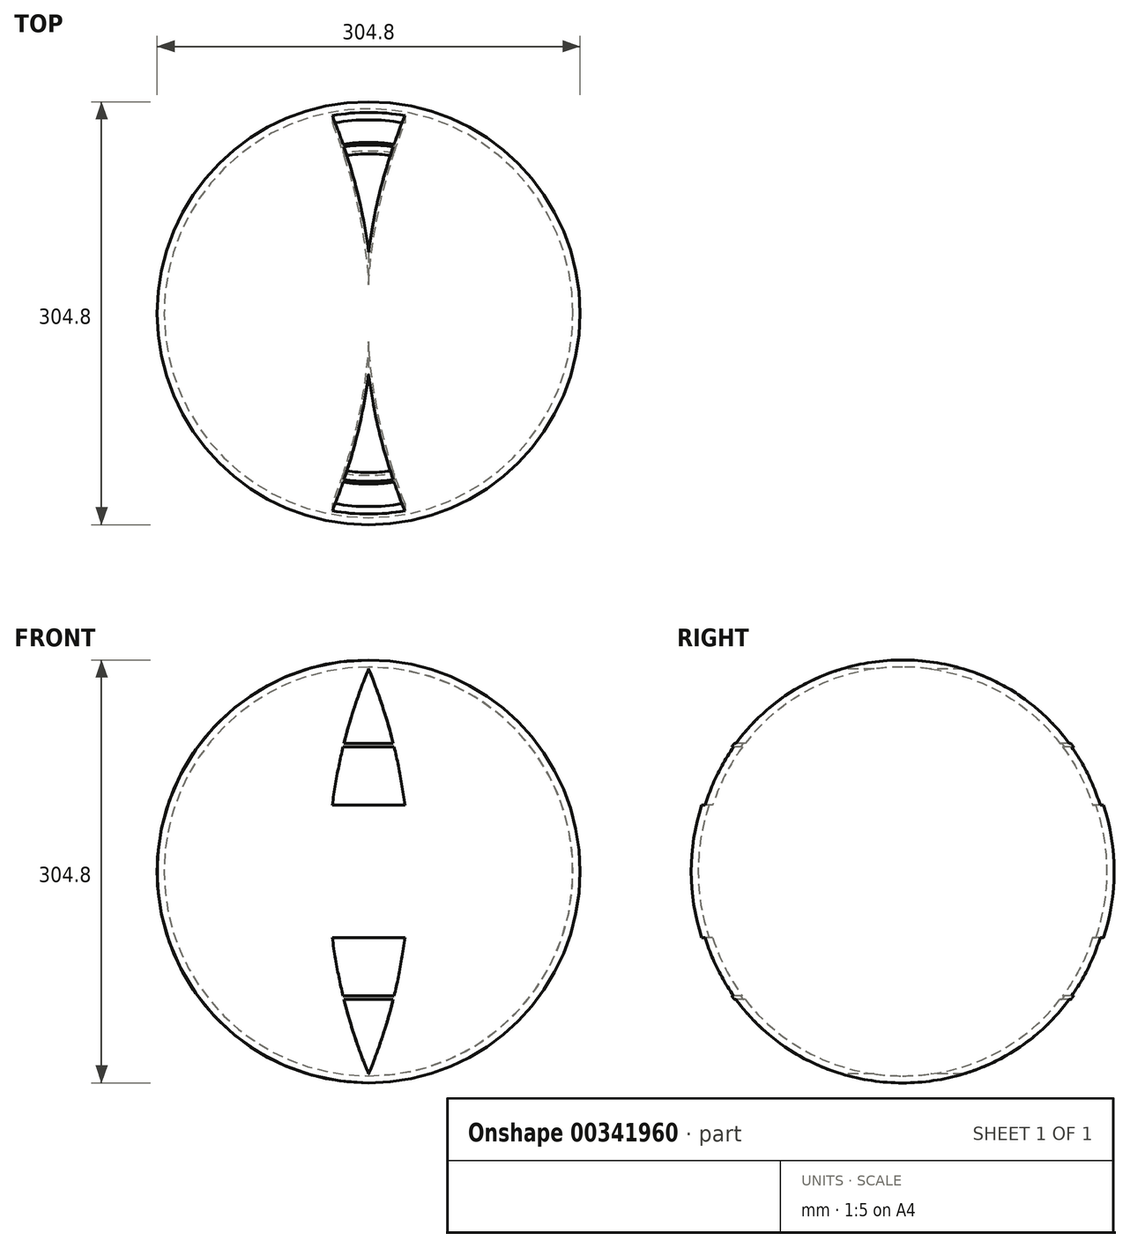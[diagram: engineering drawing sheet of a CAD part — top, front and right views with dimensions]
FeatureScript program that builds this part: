
annotation { "Feature Type Name" : "Feature", "Feature Type Description" : "" }
export const myFeature = defineFeature(function(context is Context, id is Id, definition is map)
    precondition{}
    {
        {
            var Q0;
            Q0=qCreatedBy(makeId("Front.planeOp"),FACE);
            var sketch = newSketch(context, id + "F0", { "sketchPlane" : qUnion([Q0])});
            skArc(sketch, "E0", {"start": v(0, -152.4) * mm, "mid": v(152.4, 0) * mm, "end": v(0, 152.4) * mm});
            skLineSegment(sketch, "E1", {"start": v(0, 152.4) * mm, "end": v(0, -152.4) * mm, "construction": true});
            skArc(sketch, "E2.0", {"start": v(0, -147.32) * mm, "mid": v(147.32, 0) * mm, "end": v(0, 147.32) * mm});
            skLineSegment(sketch, "E3", {"start": v(0, 152.4) * mm, "end": v(0, 147.32) * mm});
            skLineSegment(sketch, "E4", {"start": v(0, -147.32) * mm, "end": v(0, -152.4) * mm});
            skSolve(sketch);
        }
        {
            var Q0;
            Q0=makeQuery(id+"F0.imprint","IMPRINT",FACE,{"disambiguationData":[TD([[makeQuery(id+"F0.imprint","IMPRINT",EDGE,{"derivedFrom":sQuery(id+"F0.wireOp",EDGE,"E0")}),1.0]])]});
            var Q1;
            Q1=sQuery(id+"F0.wireOp",EDGE,"E0");
            var Q2;
            Q2=sQuery(id+"F0.wireOp",EDGE,"E1");
            revolve(context, id + "F1", {"entities" : qUnion([Q0]), "surfaceEntities" : qUnion([Q1]), "axis" : qUnion([Q2]), "revolveType" : RevolveType.FULL});
        }
        {
            var Q0;
            Q0=qCreatedBy(makeId("Front.planeOp"),FACE);
            cPlane(context, id + "F2", {"entities" : qUnion([Q0]), "cplaneType" : CPlaneType.OFFSET, "offset" : 152.4 * mm, "width" : 152.4 * mm, "height" : 152.4 * mm});
        }
        {
            var Q0;
            Q0=qCreatedBy(id+"F2.planeOp",FACE);
            var sketch = newSketch(context, id + "F3", { "sketchPlane" : qUnion([Q0])});
            skArc(sketch, "E5", {"start": v(0, -152.4) * mm, "mid": v(31.67, 0) * mm, "end": v(0, 152.4) * mm});
            skLineSegment(sketch, "E6", {"start": v(0, 152.4) * mm, "end": v(0, -152.4) * mm, "construction": true});
            skArc(sketch, "E7.MirrorCS", {"start": v(0, -152.4) * mm, "mid": v(-31.67, 0) * mm, "end": v(0, 152.4) * mm});
            skCircle(sketch, "E8", {"center": v(0, 0) * mm, "radius": 152.4 * mm});
            skPoint(sketch, "E9.orphan", {"position": v(28.78, 13.93) * mm});
            skLineSegment(sketch, "E10", {"start": v(-31.67, 0) * mm, "end": v(31.67, 0) * mm, "construction": true});
            skPoint(sketch, "E10.endSnap0", {"position": v(31.67, 0) * mm});
            skArc(sketch, "E11.0", {"start": v(0, -145.9) * mm, "mid": v(9.87, -119.46) * mm, "end": v(17.74, -92.35) * mm});
            skArc(sketch, "E11.1", {"start": v(0, -145.9) * mm, "mid": v(-9.87, -119.46) * mm, "end": v(-17.74, -92.35) * mm});
            skLineSegment(sketch, "E12", {"start": v(17.74, 92.35) * mm, "end": v(-17.74, 92.35) * mm});
            skLineSegment(sketch, "E13", {"start": v(18.37, 89.8) * mm, "end": v(-18.37, 89.8) * mm});
            skLineSegment(sketch, "E14", {"start": v(26.13, 47.71) * mm, "end": v(-26.13, 47.71) * mm});
            skLineSegment(sketch, "E15", {"start": v(26.44, 45.17) * mm, "end": v(-26.13, 45.17) * mm});
            skLineSegment(sketch, "E16", {"start": v(29.13, 1.27) * mm, "end": v(-29.13, 1.27) * mm});
            skLineSegment(sketch, "E17.MirrorCS", {"start": v(29.13, -1.27) * mm, "end": v(-29.13, -1.27) * mm});
            skLineSegment(sketch, "E18.MirrorCS", {"start": v(26.44, -45.17) * mm, "end": v(-26.13, -45.17) * mm});
            skLineSegment(sketch, "E19.MirrorCS", {"start": v(26.13, -47.71) * mm, "end": v(-26.13, -47.71) * mm});
            skLineSegment(sketch, "E20.MirrorCS", {"start": v(18.37, -89.8) * mm, "end": v(-18.37, -89.8) * mm});
            skLineSegment(sketch, "E21.MirrorCS", {"start": v(17.74, -92.35) * mm, "end": v(-17.74, -92.35) * mm});
            skArc(sketch, "E22.trimOffspring", {"start": v(17.74, 92.35) * mm, "mid": v(9.87, 119.46) * mm, "end": v(0, 145.9) * mm});
            skArc(sketch, "E23.trimOffspring", {"start": v(-17.74, 92.35) * mm, "mid": v(-9.87, 119.46) * mm, "end": v(0, 145.9) * mm});
            skArc(sketch, "E24.trimOffspring", {"start": v(26.13, 47.71) * mm, "mid": v(22.84, 68.87) * mm, "end": v(18.37, 89.8) * mm});
            skArc(sketch, "E25.trimOffspring", {"start": v(29.13, 1.27) * mm, "mid": v(28.42, 23.26) * mm, "end": v(26.44, 45.17) * mm});
            skArc(sketch, "E26.trimOffspring", {"start": v(-26.13, 47.71) * mm, "mid": v(-22.84, 68.87) * mm, "end": v(-18.37, 89.8) * mm});
            skPoint(sketch, "E27.orphan", {"position": v(0, 145.9) * mm});
            skPoint(sketch, "E28.orphan", {"position": v(0, -145.9) * mm});
            skArc(sketch, "E29.trimOffspring", {"start": v(18.37, -89.8) * mm, "mid": v(22.84, -68.87) * mm, "end": v(26.13, -47.71) * mm});
            skArc(sketch, "E30.trimOffspring", {"start": v(-18.37, -89.8) * mm, "mid": v(-22.84, -68.87) * mm, "end": v(-26.13, -47.71) * mm});
            skArc(sketch, "E31.trimOffspring", {"start": v(26.44, -45.17) * mm, "mid": v(28.42, -23.26) * mm, "end": v(29.13, -1.27) * mm});
            skArc(sketch, "E32.MirrorCS", {"start": v(-29.13, 1.27) * mm, "mid": v(-28.42, 23.26) * mm, "end": v(-26.44, 45.17) * mm});
            skArc(sketch, "E33.MirrorCS", {"start": v(-26.44, -45.17) * mm, "mid": v(-28.42, -23.26) * mm, "end": v(-29.13, -1.27) * mm});
            skSolve(sketch);
        }
        {
            var Q0;
            Q0=makeQuery(id+"F3.imprint","IMPRINT",FACE,{"disambiguationData":[TD([[makeQuery(id+"F3.imprint","IMPRINT",EDGE,{"derivedFrom":sQuery(id+"F3.wireOp",EDGE,"E12")}),-1.0]])]});
            var Q1;
            Q1=makeQuery(id+"F3.imprint","IMPRINT",FACE,{"disambiguationData":[TD([[makeQuery(id+"F3.imprint","IMPRINT",EDGE,{"derivedFrom":sQuery(id+"F3.wireOp",EDGE,"E13")}),1.0]])]});
            var Q2;
            Q2=makeQuery(id+"F3.imprint","IMPRINT",FACE,{"disambiguationData":[TD([[makeQuery(id+"F3.imprint","IMPRINT",EDGE,{"derivedFrom":sQuery(id+"F3.wireOp",EDGE,"E19.MirrorCS")}),1.0]])]});
            var Q3;
            Q3=makeQuery(id+"F3.imprint","IMPRINT",FACE,{"disambiguationData":[TD([[makeQuery(id+"F3.imprint","IMPRINT",EDGE,{"derivedFrom":sQuery(id+"F3.wireOp",EDGE,"E11.0")}),1.0]])]});
            extrude(context, id + "F4", {"entities" : qUnion([Q0, Q1, Q2, Q3]), "operationType" : NewBodyOperationType.REMOVE, "oppositeDirection" : true, "depth" : 330.2 * mm});
        }
        {
            var Q0;
            Q0=qCreatedBy(makeId("Top.planeOp"),FACE);
            var sketch = newSketch(context, id + "F5", { "sketchPlane" : qUnion([Q0])});
            skLineSegment(sketch, "E34", {"start": v(0, 0) * mm, "end": v(0, 230.6) * mm, "construction": true});
            skSolve(sketch);
        }
    });
